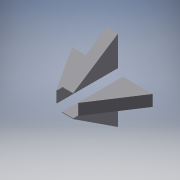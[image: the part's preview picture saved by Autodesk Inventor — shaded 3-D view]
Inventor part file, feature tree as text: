
AUTODESK INVENTOR PART (.ipt)
format: ipt  version: 2016 (Build 200138000, 138)  size: 129,536 bytes
history: native  units: in
note: dims shown in document units (in); Inventor stores cm internally (conversion verified against a paired STEP export)
features: chamfer x4, reference x2, extrude x1, sketch x1
ambient origin geometry x8: Origin, YZ Plane, XZ Plane, XY Plane, X Axis, Y Axis, Z Axis, Center Point
bodies: Solid1 (feature_tree)
feature tree (8):
  extrude  "Extrusion1"  Depth=0.2953in
  chamfer  "Chamfer1"  Distance=0.1476in
  chamfer  "Chamfer2"  Distance=0.7874in
  chamfer  "Chamfer3"  Distance=0.2953in
  chamfer  "Chamfer4"  Distance=0.7874in
  sketch  "Sketch1"  dims[d0=0.7874in d1=0.2953in d2=0.1476in d3=0.7874in d4=0.2953in d9=0.1476in d10=0.2953in d11=0.7874in d12=0.7874in d13=0.2953in d14=0.1476in d15=1.1811in d16=0.0in d17=0.7699in d18=0.125in d19=0.391in d20=0.7699in d21=0.125in d22=0.391in d23=0.7699in d24=0.125in d25=0.391in d26=0.7699in d27=0.125in d28=0.391in]
  reference  "Reference1"
  reference  "Reference2"
